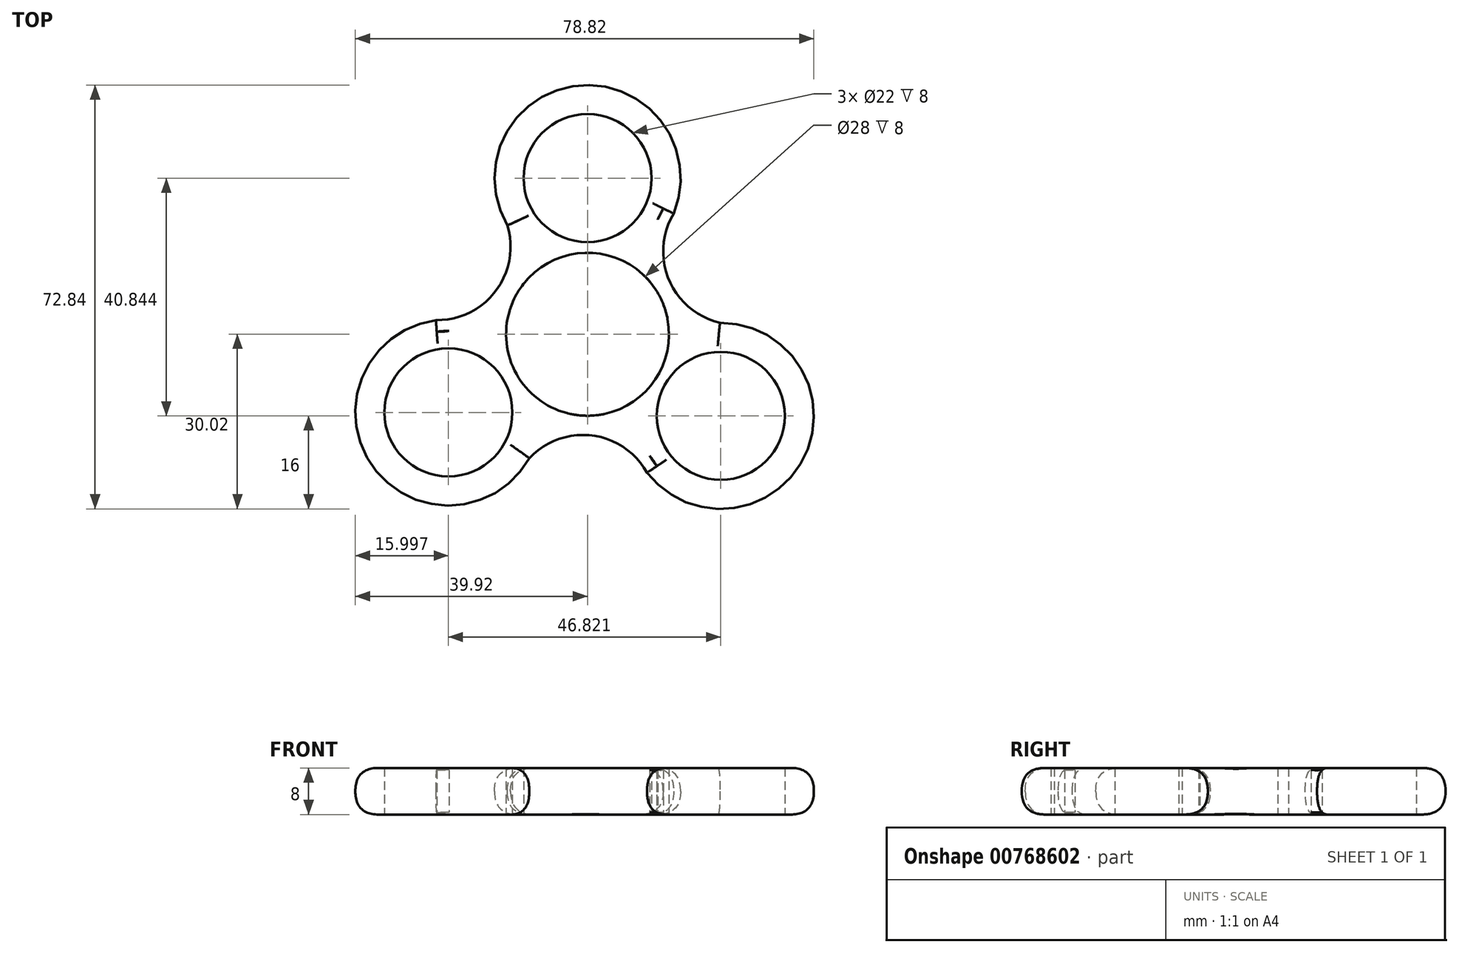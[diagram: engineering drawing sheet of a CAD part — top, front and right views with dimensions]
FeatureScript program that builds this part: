
annotation { "Feature Type Name" : "Feature", "Feature Type Description" : "" }
export const myFeature = defineFeature(function(context is Context, id is Id, definition is map)
    precondition{}
    {
        {
            var Q0;
            Q0=qCreatedBy(makeId("Top.planeOp"),FACE);
            var sketch = newSketch(context, id + "F0", { "sketchPlane" : qUnion([Q0])});
            skCircle(sketch, "E0", {"center": v(0, 0) * mm, "radius": 14 * mm});
            skCircle(sketch, "E1", {"center": v(0, 26.82) * mm, "radius": 11 * mm});
            skArc(sketch, "E2", {"start": v(12.06, 19.7) * mm, "mid": v(-0.1, 40.82) * mm, "end": v(-11.95, 19.53) * mm});
            skArc(sketch, "E3.1.0", {"start": v(-23.79, 0.57) * mm, "mid": v(-36, -20.52) * mm, "end": v(-11.63, -20.13) * mm});
            skCircle(sketch, "E3.1.1", {"center": v(-23.92, -13.43) * mm, "radius": 11 * mm});
            skArc(sketch, "E3.2.0", {"start": v(10.7, -20.9) * mm, "mid": v(35.07, -20.93) * mm, "end": v(22.56, -0.02) * mm});
            skCircle(sketch, "E3.2.1", {"center": v(22.9, -14.02) * mm, "radius": 11 * mm});
            skPoint(sketch, "E3.center", {"position": v(-0.34, -0.2) * mm});
            skArc(sketch, "E4", {"start": v(13, 21.63) * mm, "mid": v(12.24, 8.36) * mm, "end": v(22.56, -0.02) * mm});
            skArc(sketch, "E5.1.0", {"start": v(-25.92, 0.43) * mm, "mid": v(-14.05, 6.4) * mm, "end": v(-11.95, 19.53) * mm});
            skArc(sketch, "E5.2.0", {"start": v(11.9, -22.68) * mm, "mid": v(0.79, -15.39) * mm, "end": v(-11.63, -20.13) * mm});
            skArc(sketch, "E6.0", {"start": v(-23.32, 2.56) * mm, "mid": v(-37.83, -21.34) * mm, "end": v(-9.88, -21.09) * mm});
            skArc(sketch, "E7.0", {"start": v(-26.19, 2.43) * mm, "mid": v(-15.43, 7.92) * mm, "end": v(-14.24, 19.94) * mm});
            skArc(sketch, "E8.0", {"start": v(13.55, 18.31) * mm, "mid": v(0.1, 42.82) * mm, "end": v(-13.66, 18.49) * mm});
            skArc(sketch, "E9.0", {"start": v(14.87, 20.86) * mm, "mid": v(14.24, 8.79) * mm, "end": v(24.06, 1.75) * mm});
            skArc(sketch, "E10.0", {"start": v(8.75, -21.5) * mm, "mid": v(36.7, -22.11) * mm, "end": v(22.5, 1.98) * mm});
            skArc(sketch, "E11.0", {"start": v(10.3, -23.91) * mm, "mid": v(0.16, -17.34) * mm, "end": v(-10.85, -22.32) * mm});
            skSolve(sketch);
        }
        {
            var Q0;
            Q0=makeQuery(id+"F0.imprint","IMPRINT",FACE,{"disambiguationData":[TD([[makeQuery(id+"F0.imprint","IMPRINT",EDGE,{"derivedFrom":sQuery(id+"F0.wireOp",EDGE,"E0")}),-1.0]])]});
            var Q1;
            {var subQ0=sQuery(id+"F0.wireOp",EDGE,"E4");var subQ1=sQuery(id+"F0.wireOp",EDGE,"E2");var subQ2=makeQuery(id+"F0.imprint","INTERSECT",VERTEX,{"disambiguationData":[OD(0.0)],"derivedFrom":[subQ1,subQ0]});Q1=makeQuery(id+"F0.imprint","IMPRINT",FACE,{"disambiguationData":[TD([[makeQuery(id+"F0.imprint","IMPRINT",EDGE,{"disambiguationData":[TD([[subQ2,-1.0]])],"derivedFrom":subQ1}),-1.0]])]});}
            var Q2;
            Q2=makeQuery(id+"F0.imprint","IMPRINT",FACE,{"disambiguationData":[TD([[makeQuery(id+"F0.imprint","IMPRINT",EDGE,{"derivedFrom":sQuery(id+"F0.wireOp",EDGE,"E1")}),-1.0]])]});
            var Q3;
            Q3=makeQuery(id+"F0.imprint","IMPRINT",FACE,{"disambiguationData":[TD([[makeQuery(id+"F0.imprint","IMPRINT",EDGE,{"derivedFrom":sQuery(id+"F0.wireOp",EDGE,"E3.1.1")}),-1.0]])]});
            var Q4;
            Q4=makeQuery(id+"F0.imprint","IMPRINT",FACE,{"disambiguationData":[TD([[makeQuery(id+"F0.imprint","IMPRINT",EDGE,{"derivedFrom":sQuery(id+"F0.wireOp",EDGE,"E3.2.1")}),-1.0]])]});
            extrude(context, id + "F1", {"entities" : qUnion([Q0, Q1, Q2, Q3, Q4]), "endBound" : BoundingType.SYMMETRIC, "depth" : 8 * mm, "offsetDistance" : 25 * mm});
        }
        {
            var Q0;
            Q0=makeQuery(id+"F1.opExtrude","CAP_EDGE",EDGE,{"disambiguationData":[OSD([sQuery(id+"F0.wireOp",EDGE,"E7.0")])],"isStart":false});
            var Q1;
            Q1=makeQuery(id+"F1.opExtrude","CAP_EDGE",EDGE,{"disambiguationData":[OSD([sQuery(id+"F0.wireOp",EDGE,"E11.0")])],"isStart":false});
            var Q2;
            Q2=makeQuery(id+"F1.opExtrude","CAP_EDGE",EDGE,{"disambiguationData":[OSD([sQuery(id+"F0.wireOp",EDGE,"E9.0")])],"isStart":false});
            var Q3;
            Q3=makeQuery(id+"F1.opExtrude","CAP_EDGE",EDGE,{"disambiguationData":[OSD([sQuery(id+"F0.wireOp",EDGE,"E8.0")])],"isStart":false});
            var Q4;
            Q4=makeQuery(id+"F1.opExtrude","CAP_EDGE",EDGE,{"disambiguationData":[OSD([sQuery(id+"F0.wireOp",EDGE,"E10.0")])],"isStart":false});
            var Q5;
            Q5=makeQuery(id+"F1.opExtrude","CAP_EDGE",EDGE,{"disambiguationData":[OSD([sQuery(id+"F0.wireOp",EDGE,"E6.0")])],"isStart":false});
            var Q6;
            Q6=makeQuery(id+"F1.opExtrude","CAP_EDGE",EDGE,{"disambiguationData":[OSD([sQuery(id+"F0.wireOp",EDGE,"E11.0")])],"isStart":true});
            var Q7;
            Q7=makeQuery(id+"F1.opExtrude","CAP_EDGE",EDGE,{"disambiguationData":[OSD([sQuery(id+"F0.wireOp",EDGE,"E7.0")])],"isStart":true});
            var Q8;
            Q8=makeQuery(id+"F1.opExtrude","CAP_EDGE",EDGE,{"disambiguationData":[OSD([sQuery(id+"F0.wireOp",EDGE,"E9.0")])],"isStart":true});
            var Q9;
            Q9=makeQuery(id+"F1.opExtrude","CAP_EDGE",EDGE,{"disambiguationData":[OSD([sQuery(id+"F0.wireOp",EDGE,"E10.0")])],"isStart":true});
            var Q10;
            Q10=makeQuery(id+"F1.opExtrude","CAP_EDGE",EDGE,{"disambiguationData":[OSD([sQuery(id+"F0.wireOp",EDGE,"E6.0")])],"isStart":true});
            var Q11;
            Q11=makeQuery(id+"F1.opExtrude","CAP_EDGE",EDGE,{"disambiguationData":[OSD([sQuery(id+"F0.wireOp",EDGE,"E8.0")])],"isStart":true});
            fillet(context, id + "F2", {"entities" : qUnion([Q0, Q1, Q2, Q3, Q4, Q5, Q6, Q7, Q8, Q9, Q10, Q11]), "radius" : 4 * mm, "tangentPropagation" : true, "rho" : 0.5, "crossSection" : FilletCrossSection.CONIC, "allowEdgeOverflow" : false});
        }
    });
